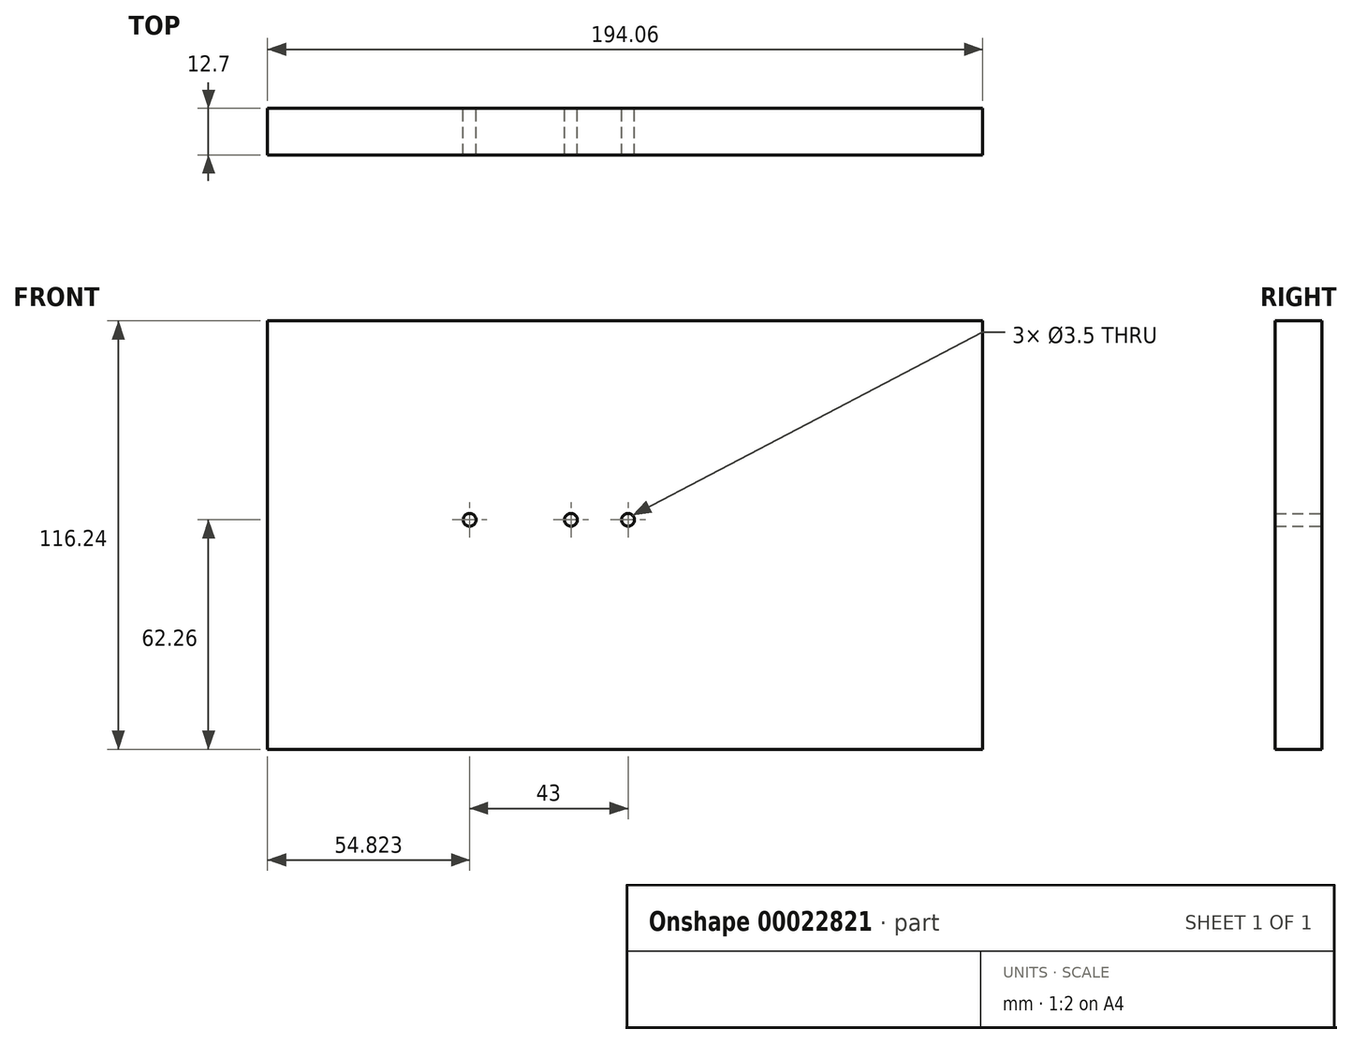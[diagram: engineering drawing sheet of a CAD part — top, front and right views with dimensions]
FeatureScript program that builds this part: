
annotation { "Feature Type Name" : "Feature", "Feature Type Description" : "" }
export const myFeature = defineFeature(function(context is Context, id is Id, definition is map)
    precondition{}
    {
        {
            var Q0;
            Q0=qCreatedBy(makeId("Front.planeOp"),FACE);
            var sketch = newSketch(context, id + "F0", { "sketchPlane" : qUnion([Q0])});
            skLineSegment(sketch, "E0.rect.bottom", {"start": v(-97.03, 53.98) * mm, "end": v(97.03, 53.98) * mm});
            skLineSegment(sketch, "E0.rect.top", {"start": v(-97.03, -62.26) * mm, "end": v(97.03, -62.26) * mm});
            skLineSegment(sketch, "E0.rect.left", {"start": v(-97.03, 53.98) * mm, "end": v(-97.03, -62.26) * mm});
            skLineSegment(sketch, "E0.rect.right", {"start": v(97.03, 53.98) * mm, "end": v(97.03, -62.26) * mm});
            skPoint(sketch, "E0.rect.middle", {"position": v(0, -4.14) * mm});
            skCircle(sketch, "E1", {"center": v(-42.2, 0) * mm, "radius": 1.75 * mm});
            skLineSegment(sketch, "E2", {"start": v(-42.2, 0) * mm, "end": v(-14.7, 0) * mm});
            skLineSegment(sketch, "E3", {"start": v(-14.7, 0) * mm, "end": v(0.8, 0) * mm});
            skCircle(sketch, "E4", {"center": v(-14.7, 0) * mm, "radius": 1.75 * mm});
            skCircle(sketch, "E5", {"center": v(0.8, 0) * mm, "radius": 1.75 * mm});
            skSolve(sketch);
        }
        {
            var Q0;
            Q0=makeQuery(id+"F0.imprint","IMPRINT",FACE,{"disambiguationData":[TD([[makeQuery(id+"F0.imprint","IMPRINT",EDGE,{"derivedFrom":sQuery(id+"F0.wireOp",EDGE,"E0.rect.bottom")}),-1.0]])]});
            extrude(context, id + "F1", {"entities" : qUnion([Q0]), "depth" : 12.7 * mm});
        }
    });
